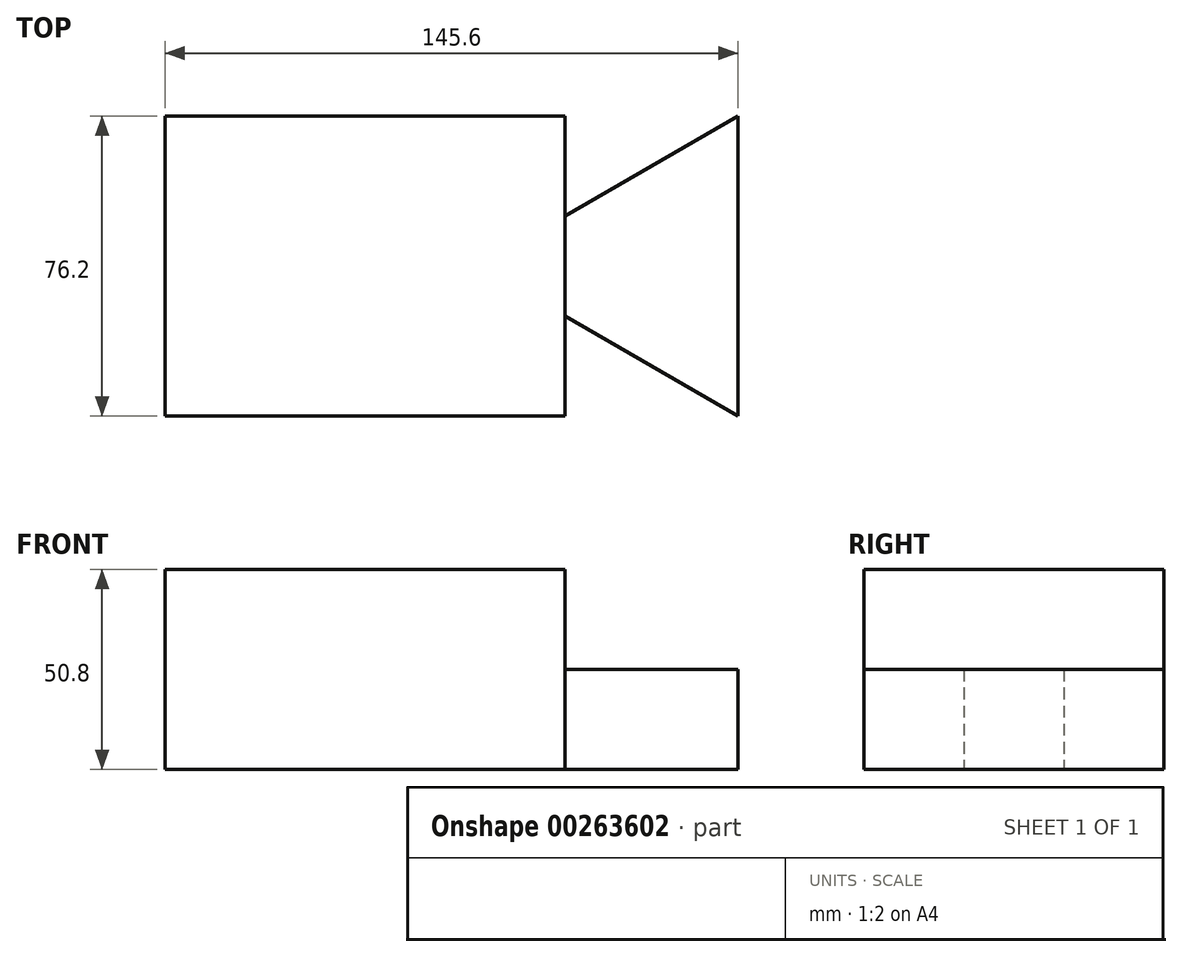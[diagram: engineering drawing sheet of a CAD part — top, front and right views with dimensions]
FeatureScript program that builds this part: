
annotation { "Feature Type Name" : "Feature", "Feature Type Description" : "" }
export const myFeature = defineFeature(function(context is Context, id is Id, definition is map)
    precondition{}
    {
        {
            var Q0;
            Q0=qCreatedBy(makeId("Top.planeOp"),FACE);
            var sketch = newSketch(context, id + "F0", { "sketchPlane" : qUnion([Q0])});
            skLineSegment(sketch, "E0.bottom", {"start": v(-75.12, 0) * mm, "end": v(26.48, 0) * mm});
            skLineSegment(sketch, "E0.top", {"start": v(-75.12, 76.2) * mm, "end": v(26.48, 76.2) * mm});
            skLineSegment(sketch, "E0.left", {"start": v(-75.12, 0) * mm, "end": v(-75.12, 76.2) * mm});
            skLineSegment(sketch, "E0.right", {"start": v(26.48, 0) * mm, "end": v(26.48, 76.2) * mm});
            skLineSegment(sketch, "E1", {"start": v(26.48, 76.2) * mm, "end": v(26.48, 50.8) * mm});
            skLineSegment(sketch, "E2", {"start": v(26.48, 0) * mm, "end": v(26.48, 25.4) * mm});
            skLineSegment(sketch, "E3", {"start": v(26.48, 50.8) * mm, "end": v(70.48, 76.2) * mm});
            skLineSegment(sketch, "E4", {"start": v(26.48, 25.4) * mm, "end": v(70.48, 0) * mm});
            skLineSegment(sketch, "E5", {"start": v(70.48, 76.2) * mm, "end": v(70.48, 0) * mm});
            skSolve(sketch);
        }
        {
            var Q0;
            Q0=makeQuery(id+"F0.imprint","IMPRINT",FACE,{"disambiguationData":[TD([[makeQuery(id+"F0.imprint","IMPRINT",EDGE,{"derivedFrom":sQuery(id+"F0.wireOp",EDGE,"E0.bottom")}),1.0]])]});
            extrude(context, id + "F1", {"entities" : qUnion([Q0]), "depth" : 50.8 * mm});
        }
        {
            var Q0;
            Q0=makeQuery(id+"F0.imprint","IMPRINT",FACE,{"disambiguationData":[TD([[makeQuery(id+"F0.imprint","IMPRINT",EDGE,{"derivedFrom":sQuery(id+"F0.wireOp",EDGE,"E0.right")}),-1.0]])]});
            extrude(context, id + "F2", {"entities" : qUnion([Q0]), "operationType" : NewBodyOperationType.ADD, "depth" : 25.4 * mm});
        }
    });
